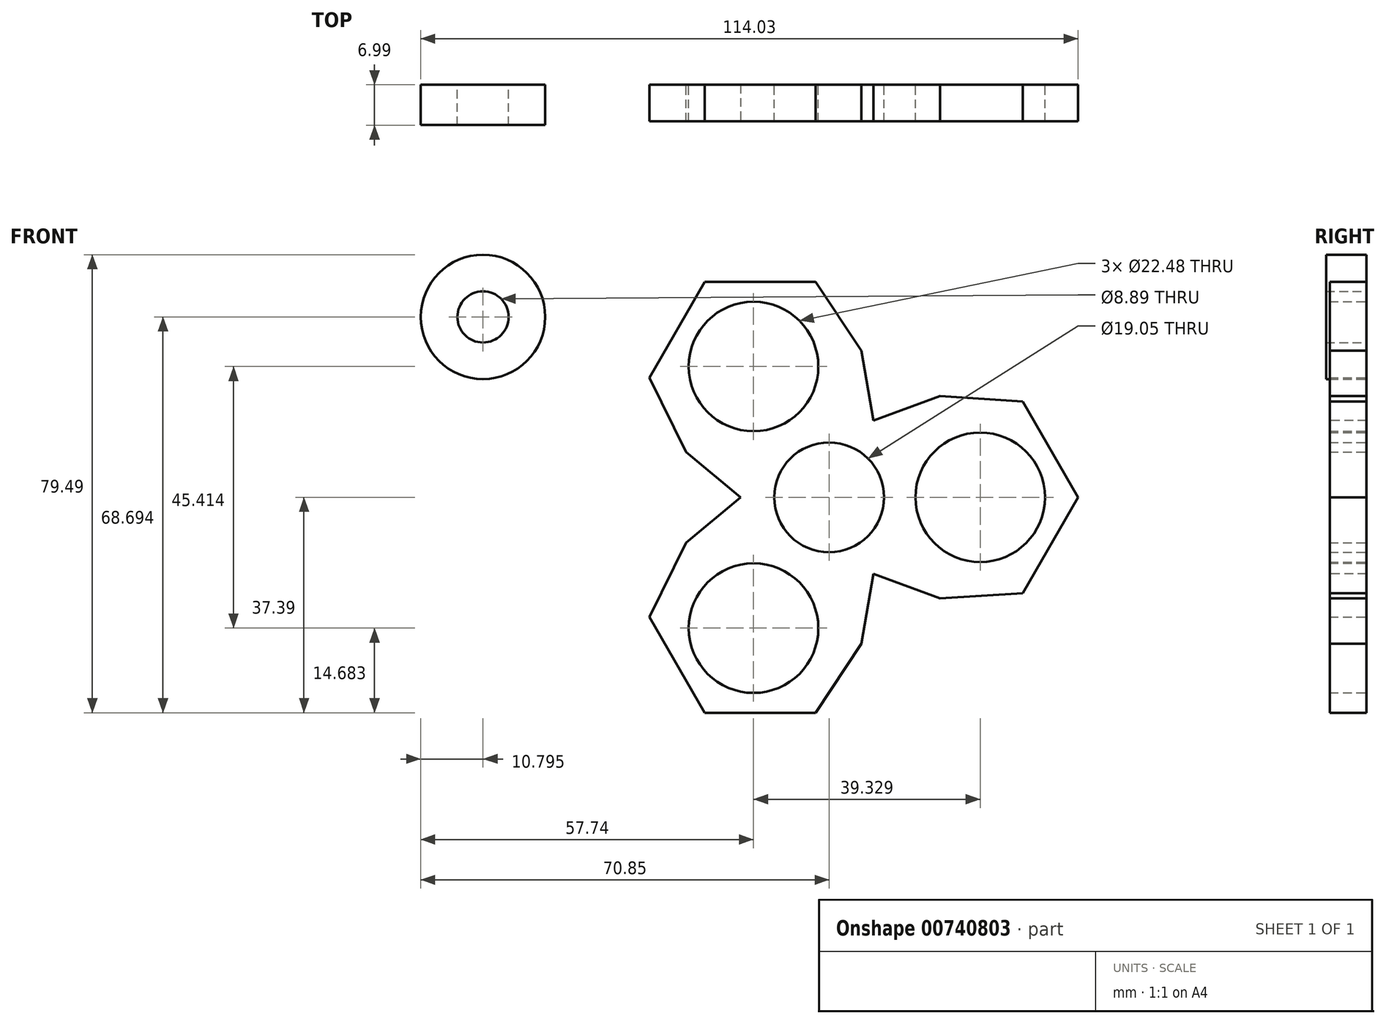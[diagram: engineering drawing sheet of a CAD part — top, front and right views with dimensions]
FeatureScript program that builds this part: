
annotation { "Feature Type Name" : "Feature", "Feature Type Description" : "" }
export const myFeature = defineFeature(function(context is Context, id is Id, definition is map)
    precondition{}
    {
        {
            var Q0;
            Q0=qCreatedBy(makeId("Front.planeOp"),FACE);
            var sketch = newSketch(context, id + "F0", { "sketchPlane" : qUnion([Q0])});
            skLineSegment(sketch, "E0.0", {"start": v(33.57, 16.65) * mm, "end": v(42.45, 1.27) * mm});
            skLineSegment(sketch, "E0.1", {"start": v(42.45, -1.27) * mm, "end": v(33.57, -16.65) * mm});
            skLineSegment(sketch, "E0.2", {"start": v(-2.36, -37.4) * mm, "end": v(-20.12, -37.4) * mm});
            skLineSegment(sketch, "E0.3", {"start": v(-22.32, -36.12) * mm, "end": v(-31.2, -20.75) * mm});
            skLineSegment(sketch, "E0.4", {"start": v(-31.2, 20.75) * mm, "end": v(-22.32, 36.12) * mm});
            skLineSegment(sketch, "E0.5", {"start": v(-20.12, 37.4) * mm, "end": v(-2.36, 37.4) * mm});
            skPoint(sketch, "E0.0.midPoint", {"position": v(32.38, 18.7) * mm});
            skPoint(sketch, "E1.visualSharp", {"position": v(-43.18, 0) * mm});
            skPoint(sketch, "E2.visualSharp", {"position": v(-21.59, 37.4) * mm});
            skArc(sketch, "E2.filletArc", {"start": v(-20.12, 37.4) * mm, "mid": v(-21.4, 37.05) * mm, "end": v(-22.32, 36.12) * mm});
            skPoint(sketch, "E3.visualSharp", {"position": v(21.6, 37.4) * mm});
            skPoint(sketch, "E4.visualSharp", {"position": v(43.18, 0) * mm});
            skArc(sketch, "E4.filletArc", {"start": v(42.45, -1.27) * mm, "mid": v(42.79, 0) * mm, "end": v(42.45, 1.27) * mm});
            skPoint(sketch, "E5.visualSharp", {"position": v(21.6, -37.4) * mm});
            skPoint(sketch, "E6.visualSharp", {"position": v(-21.59, -37.4) * mm});
            skArc(sketch, "E6.filletArc", {"start": v(-22.32, -36.12) * mm, "mid": v(-21.4, -37.05) * mm, "end": v(-20.12, -37.4) * mm});
            skCircle(sketch, "E7", {"center": v(0, 0) * mm, "radius": 9.53 * mm});
            skCircle(sketch, "E8", {"center": v(-13.1, -22.7) * mm, "radius": 11.24 * mm});
            skCircle(sketch, "E9.MirrorC", {"center": v(26.22, 0) * mm, "radius": 11.24 * mm});
            skCircle(sketch, "E10.MirrorC", {"center": v(-13.1, 22.7) * mm, "radius": 11.24 * mm});
            skLineSegment(sketch, "E11.trimOffspring", {"start": v(-21.4, -37.05) * mm, "end": v(-21.59, -37.4) * mm});
            skLineSegment(sketch, "E12", {"start": v(-2.36, -37.4) * mm, "end": v(-2.32, -37.32) * mm});
            skLineSegment(sketch, "E13", {"start": v(5.58, -25.44) * mm, "end": v(7.68, -13.3) * mm});
            skLineSegment(sketch, "E14.MirrorCS", {"start": v(19.24, -17.55) * mm, "end": v(7.68, -13.3) * mm});
            skLineSegment(sketch, "E15.MirrorCS", {"start": v(19.24, 17.55) * mm, "end": v(7.68, 13.3) * mm});
            skLineSegment(sketch, "E16.MirrorCS", {"start": v(33.57, 16.65) * mm, "end": v(19.24, 17.55) * mm});
            skLineSegment(sketch, "E17.MirrorCS", {"start": v(5.58, 25.44) * mm, "end": v(7.68, 13.3) * mm});
            skLineSegment(sketch, "E18.MirrorCS", {"start": v(-2.36, 37.4) * mm, "end": v(5.58, 25.44) * mm});
            skLineSegment(sketch, "E19.MirrorCS", {"start": v(33.57, -16.65) * mm, "end": v(42.45, -1.27) * mm});
            skPoint(sketch, "E20.MirrorP", {"position": v(21.59, -37.4) * mm});
            skPoint(sketch, "E21.MirrorCS.end.orphan", {"position": v(42.45, -73.52) * mm});
            skPoint(sketch, "E21.MirrorCS.start.orphan", {"position": v(22.32, -38.67) * mm});
            skPoint(sketch, "E22.MirrorCS.end.orphan", {"position": v(20.12, -37.4) * mm});
            skPoint(sketch, "E22.MirrorCS.start.orphan", {"position": v(0, -37.4) * mm});
            skPoint(sketch, "E23.orphan", {"position": v(22.32, -36.12) * mm});
            skLineSegment(sketch, "E24.MirrorCS", {"start": v(-24.82, -7.89) * mm, "end": v(-15.35, 0) * mm});
            skLineSegment(sketch, "E25.MirrorCS", {"start": v(-24.82, 7.89) * mm, "end": v(-15.35, 0) * mm});
            skLineSegment(sketch, "E26.MirrorCS", {"start": v(-31.2, 20.75) * mm, "end": v(-31.16, 20.67) * mm});
            skLineSegment(sketch, "E27.MirrorCS", {"start": v(-31.2, -20.75) * mm, "end": v(-31.16, -20.67) * mm});
            skPoint(sketch, "E1.filletArc.end.orphan", {"position": v(-42.45, -1.27) * mm});
            skLineSegment(sketch, "E28", {"start": v(7.68, 13.3) * mm, "end": v(19.24, 17.55) * mm});
            skLineSegment(sketch, "E29", {"start": v(-15.35, 0) * mm, "end": v(-24.82, 7.89) * mm});
            skCircle(sketch, "E30.cCircle", {"center": v(0, 0) * mm, "radius": 37.4 * mm, "construction": true});
            skLineSegment(sketch, "E30.0", {"start": v(33.57, 16.65) * mm, "end": v(43.18, 0) * mm});
            skLineSegment(sketch, "E30.1", {"start": v(43.18, 0) * mm, "end": v(32.39, -18.7) * mm});
            skLineSegment(sketch, "E30.3", {"start": v(-21.59, -37.4) * mm, "end": v(-32.38, -18.7) * mm});
            skLineSegment(sketch, "E30.4", {"start": v(-32.39, 18.7) * mm, "end": v(-21.6, 37.4) * mm});
            skLineSegment(sketch, "E30.5", {"start": v(-21.6, 37.4) * mm, "end": v(-2.36, 37.4) * mm});
            skPoint(sketch, "E31.MirrorCS.start.orphan", {"position": v(16.1, -34.22) * mm});
            skPoint(sketch, "E32.0.start.orphan", {"position": v(21.6, -31.04) * mm});
            skLineSegment(sketch, "E33.trimOffspring", {"start": v(1.86, -31.04) * mm, "end": v(5.58, -25.44) * mm});
            skLineSegment(sketch, "E34.trimOffspring", {"start": v(25.96, -17.13) * mm, "end": v(19.24, -17.55) * mm});
            skPoint(sketch, "E35.orphan", {"position": v(21.59, 37.4) * mm});
            skPoint(sketch, "E36.orphan", {"position": v(-31.05, -2.77) * mm});
            skPoint(sketch, "E37.orphan", {"position": v(-31.05, 2.77) * mm});
            skPoint(sketch, "E38.orphan", {"position": v(-23.02, 11.15) * mm});
            skPoint(sketch, "E39.orphan", {"position": v(-23.02, -11.15) * mm});
            skLineSegment(sketch, "E40.trimOffspring", {"start": v(-24.86, -7.96) * mm, "end": v(-24.82, -7.89) * mm});
            skLineSegment(sketch, "E41.trimOffspring", {"start": v(-24.86, 7.96) * mm, "end": v(-24.82, 7.89) * mm});
            skLineSegment(sketch, "E42", {"start": v(19.24, -17.55) * mm, "end": v(33.57, -16.65) * mm});
            skLineSegment(sketch, "E43", {"start": v(5.58, -25.44) * mm, "end": v(-2.32, -37.32) * mm});
            skLineSegment(sketch, "E44.trimOffspring", {"start": v(0, -37.4) * mm, "end": v(-21.59, -37.4) * mm});
            skLineSegment(sketch, "E45", {"start": v(0, 0) * mm, "end": v(-13.1, -22.7) * mm});
            skLineSegment(sketch, "E46.MirrorCS", {"start": v(-24.82, -7.89) * mm, "end": v(-31.16, -20.67) * mm});
            skLineSegment(sketch, "E47.MirrorCS", {"start": v(-27.81, 13.92) * mm, "end": v(-24.82, 7.89) * mm});
            skLineSegment(sketch, "E48.MirrorCS", {"start": v(-24.82, 7.89) * mm, "end": v(-31.2, 20.75) * mm});
            skSolve(sketch);
        }
        {
            var Q0;
            Q0 = qSketchRegion(id + "F0", true);
            extrude(context, id + "F1", {"entities" : qUnion([Q0]), "depth" : 6.35 * mm, "offsetDistance" : 25.4 * mm});
        }
        {
            var Q0;
            Q0=qCreatedBy(makeId("Front.planeOp"),FACE);
            var sketch = newSketch(context, id + "F2", { "sketchPlane" : qUnion([Q0])});
            skCircle(sketch, "E49", {"center": v(-60.05, 31.3) * mm, "radius": 4.45 * mm});
            skCircle(sketch, "E50", {"center": v(-60.05, 31.3) * mm, "radius": 10.8 * mm});
            skSolve(sketch);
        }
        {
            var Q0;
            Q0 = qSketchRegion(id + "F2", true);
            extrude(context, id + "F3", {"entities" : qUnion([Q0]), "depth" : 7 * mm, "offsetDistance" : 25.4 * mm});
        }
    });
